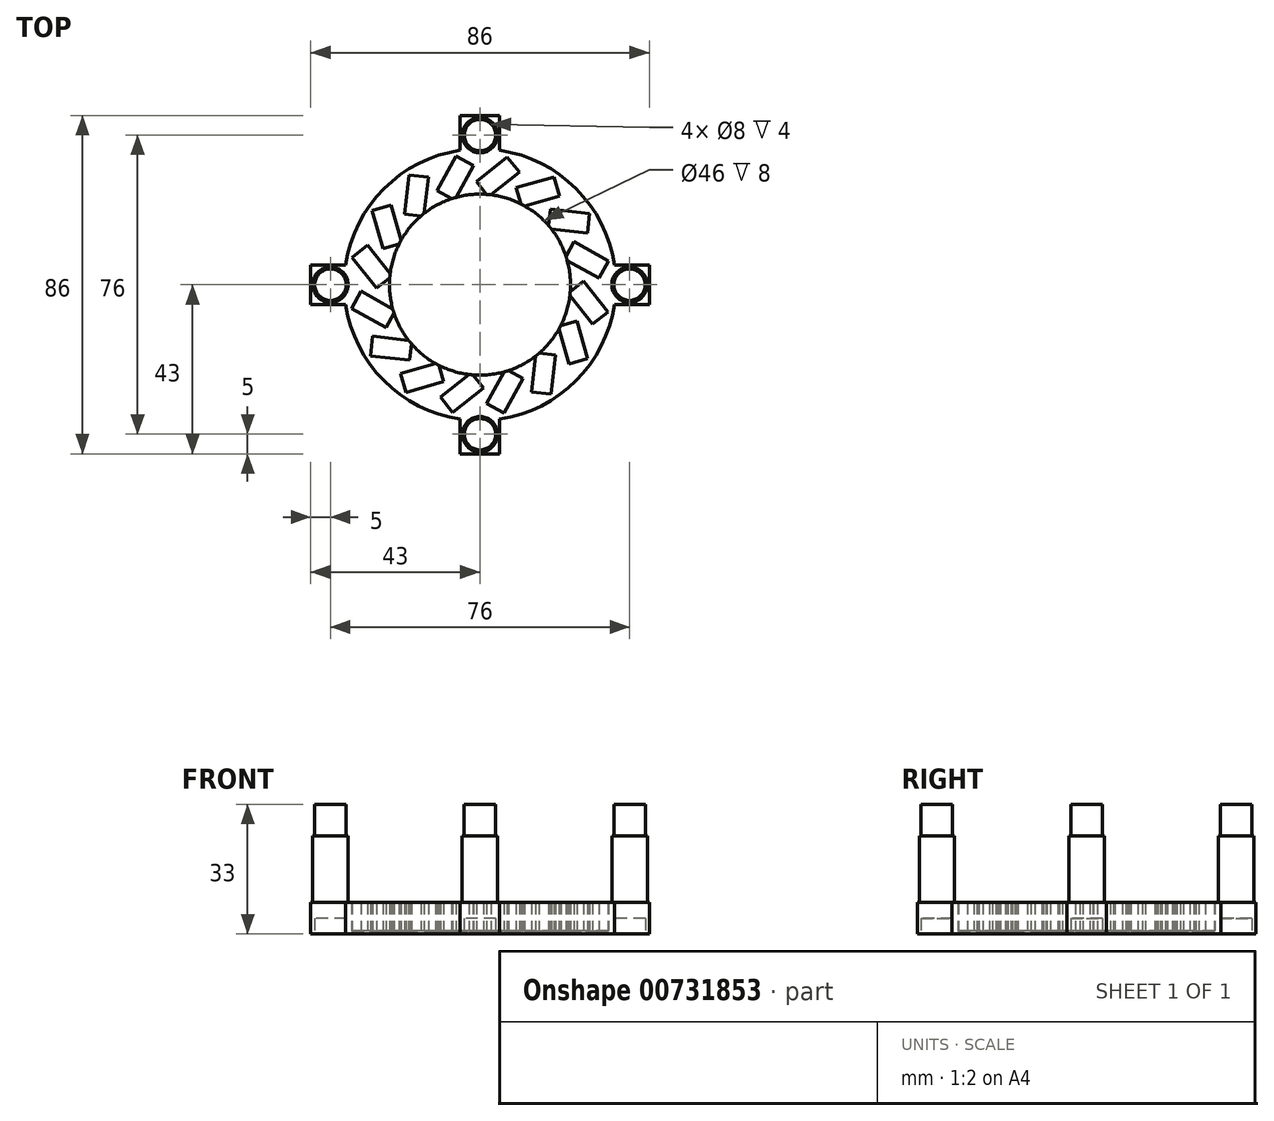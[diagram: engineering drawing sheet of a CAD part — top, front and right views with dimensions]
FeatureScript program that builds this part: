
annotation { "Feature Type Name" : "Feature", "Feature Type Description" : "" }
export const myFeature = defineFeature(function(context is Context, id is Id, definition is map)
    precondition{}
    {
        {
            var Q0;
            Q0=qCreatedBy(makeId("Top.planeOp"),FACE);
            var sketch = newSketch(context, id + "F0", { "sketchPlane" : qUnion([Q0])});
            skCircle(sketch, "E0", {"center": v(0, 0) * mm, "radius": 23 * mm});
            skCircle(sketch, "E1", {"center": v(0, 0) * mm, "radius": 34 * mm});
            skLineSegment(sketch, "E2", {"start": v(0, 0) * mm, "end": v(0.79, 29.99) * mm, "construction": true});
            skLineSegment(sketch, "E3.bottom", {"start": v(8.46, 30.52) * mm, "end": v(10.02, 28.56) * mm});
            skLineSegment(sketch, "E3.top", {"start": v(0.64, 24.3) * mm, "end": v(2.2, 22.34) * mm});
            skLineSegment(sketch, "E3.right", {"start": v(10.02, 28.56) * mm, "end": v(2.2, 22.34) * mm});
            skLineSegment(sketch, "E4.MirrorCS", {"start": v(6.9, 32.47) * mm, "end": v(-0.92, 26.25) * mm});
            skLineSegment(sketch, "E5.MirrorCS", {"start": v(0.64, 24.3) * mm, "end": v(-0.92, 26.25) * mm});
            skLineSegment(sketch, "E6.MirrorCS", {"start": v(8.46, 30.52) * mm, "end": v(6.9, 32.47) * mm});
            skLineSegment(sketch, "E7", {"start": v(0, 0) * mm, "end": v(35, 0) * mm, "construction": true});
            skPoint(sketch, "E8", {"position": v(0.6, 23) * mm});
            skSolve(sketch);
        }
        {
            var Q0;
            Q0=qCreatedBy(makeId("Top.planeOp"),FACE);
            var sketch = newSketch(context, id + "F1", { "sketchPlane" : qUnion([Q0])});
            skArc(sketch, "E9", {"start": v(-34.4, -2.7) * mm, "mid": v(-24.4, -24.4) * mm, "end": v(-2.7, -34.4) * mm});
            skCircle(sketch, "E10", {"center": v(0, 0) * mm, "radius": 23 * mm});
            skArc(sketch, "E11", {"start": v(-33.94, -1.95) * mm, "mid": v(-24.04, -24.04) * mm, "end": v(-1.95, -33.94) * mm});
            skLineSegment(sketch, "E12", {"start": v(0, 0) * mm, "end": v(34, 0) * mm, "construction": true});
            skCircle(sketch, "E13", {"center": v(0, 38) * mm, "radius": 4 * mm});
            skCircle(sketch, "E14", {"center": v(0, 38) * mm, "radius": 4.5 * mm});
            skLineSegment(sketch, "E15", {"start": v(0, 42.5) * mm, "end": v(0, 43) * mm});
            skLineSegment(sketch, "E16", {"start": v(0, 43) * mm, "end": v(5, 43) * mm});
            skLineSegment(sketch, "E17", {"start": v(5, 43) * mm, "end": v(5, 34.14) * mm});
            skLineSegment(sketch, "E18.MirrorCS", {"start": v(0, 43) * mm, "end": v(-5, 43) * mm});
            skLineSegment(sketch, "E19.MirrorCS", {"start": v(-5, 43) * mm, "end": v(-5, 34.14) * mm});
            skLineSegment(sketch, "E20.1.0", {"start": v(-43, 0) * mm, "end": v(-43, 5) * mm});
            skLineSegment(sketch, "E20.1.1", {"start": v(-43, 5) * mm, "end": v(-34.14, 5) * mm});
            skLineSegment(sketch, "E20.1.2", {"start": v(-43, 0) * mm, "end": v(-43, -5) * mm});
            skLineSegment(sketch, "E20.1.3", {"start": v(-43, -5) * mm, "end": v(-34.14, -5) * mm});
            skCircle(sketch, "E20.1.4", {"center": v(-38, 0) * mm, "radius": 4.5 * mm});
            skCircle(sketch, "E20.1.5", {"center": v(-38, 0) * mm, "radius": 4 * mm});
            skLineSegment(sketch, "E20.2.0", {"start": v(0, -43) * mm, "end": v(-5, -43) * mm});
            skLineSegment(sketch, "E20.2.1", {"start": v(-5, -43) * mm, "end": v(-5, -34.14) * mm});
            skLineSegment(sketch, "E20.2.2", {"start": v(0, -43) * mm, "end": v(5, -43) * mm});
            skLineSegment(sketch, "E20.2.3", {"start": v(5, -43) * mm, "end": v(5, -34.14) * mm});
            skCircle(sketch, "E20.2.4", {"center": v(0, -38) * mm, "radius": 4.5 * mm});
            skCircle(sketch, "E20.2.5", {"center": v(0, -38) * mm, "radius": 4 * mm});
            skLineSegment(sketch, "E20.3.0", {"start": v(43, 0) * mm, "end": v(43, -5) * mm});
            skLineSegment(sketch, "E20.3.1", {"start": v(43, -5) * mm, "end": v(34.14, -5) * mm});
            skLineSegment(sketch, "E20.3.2", {"start": v(43, 0) * mm, "end": v(43, 5) * mm});
            skLineSegment(sketch, "E20.3.3", {"start": v(43, 5) * mm, "end": v(34.14, 5) * mm});
            skCircle(sketch, "E20.3.4", {"center": v(38, 0) * mm, "radius": 4.5 * mm});
            skCircle(sketch, "E20.3.5", {"center": v(38, 0) * mm, "radius": 4 * mm});
            skArc(sketch, "E21.trimOffspring", {"start": v(33.94, 1.95) * mm, "mid": v(24.04, 24.04) * mm, "end": v(1.95, 33.94) * mm});
            skArc(sketch, "E22.trimOffspring", {"start": v(34.4, 2.7) * mm, "mid": v(24.4, 24.4) * mm, "end": v(2.7, 34.4) * mm});
            skArc(sketch, "E23.trimOffspring", {"start": v(-2.7, 34.4) * mm, "mid": v(-24.4, 24.4) * mm, "end": v(-34.4, 2.7) * mm});
            skArc(sketch, "E24.trimOffspring", {"start": v(2.7, -34.4) * mm, "mid": v(24.4, -24.4) * mm, "end": v(34.4, -2.7) * mm});
            skArc(sketch, "E25.trimOffspring", {"start": v(1.95, -33.94) * mm, "mid": v(24.04, -24.04) * mm, "end": v(33.94, -1.95) * mm});
            skArc(sketch, "E26.trimOffspring", {"start": v(-1.95, 33.94) * mm, "mid": v(-24.04, 24.04) * mm, "end": v(-33.94, 1.95) * mm});
            skLineSegment(sketch, "E27.0.0", {"start": v(-0.92, 26.25) * mm, "end": v(0.64, 24.3) * mm});
            skLineSegment(sketch, "E27.0.1", {"start": v(0.64, 24.3) * mm, "end": v(1.71, 22.94) * mm});
            skLineSegment(sketch, "E27.0.3", {"start": v(2.81, 22.83) * mm, "end": v(10.02, 28.56) * mm});
            skLineSegment(sketch, "E27.0.4", {"start": v(10.02, 28.56) * mm, "end": v(8.46, 30.52) * mm});
            skLineSegment(sketch, "E27.0.5", {"start": v(8.46, 30.52) * mm, "end": v(6.9, 32.47) * mm});
            skLineSegment(sketch, "E27.0.6", {"start": v(6.9, 32.47) * mm, "end": v(-0.92, 26.25) * mm});
            skLineSegment(sketch, "E28.0.0", {"start": v(2.2, 22.34) * mm, "end": v(2.81, 22.83) * mm});
            skLineSegment(sketch, "E28.0.2", {"start": v(1.71, 22.94) * mm, "end": v(2.2, 22.34) * mm});
            skLineSegment(sketch, "E29.1.0", {"start": v(-6.05, 32.64) * mm, "end": v(-10.9, 23.9) * mm});
            skLineSegment(sketch, "E29.1.1", {"start": v(-3.86, 31.43) * mm, "end": v(-6.05, 32.64) * mm});
            skLineSegment(sketch, "E29.1.2", {"start": v(-1.67, 30.22) * mm, "end": v(-3.86, 31.43) * mm});
            skLineSegment(sketch, "E29.1.3", {"start": v(-6.14, 22.17) * mm, "end": v(-1.67, 30.22) * mm});
            skLineSegment(sketch, "E29.1.4", {"start": v(-8.7, 22.69) * mm, "end": v(-7.2, 21.85) * mm});
            skLineSegment(sketch, "E29.1.5", {"start": v(-10.9, 23.9) * mm, "end": v(-8.7, 22.69) * mm});
            skLineSegment(sketch, "E29.1.6", {"start": v(-6.52, 21.47) * mm, "end": v(-6.14, 22.17) * mm});
            skLineSegment(sketch, "E29.1.7", {"start": v(-7.2, 21.85) * mm, "end": v(-6.52, 21.47) * mm});
            skLineSegment(sketch, "E29.2.0", {"start": v(-18.08, 27.85) * mm, "end": v(-19.21, 17.9) * mm});
            skLineSegment(sketch, "E29.2.1", {"start": v(-15.6, 27.56) * mm, "end": v(-18.08, 27.85) * mm});
            skLineSegment(sketch, "E29.2.2", {"start": v(-13.11, 27.28) * mm, "end": v(-15.6, 27.56) * mm});
            skLineSegment(sketch, "E29.2.3", {"start": v(-14.15, 18.13) * mm, "end": v(-13.11, 27.28) * mm});
            skLineSegment(sketch, "E29.2.4", {"start": v(-16.73, 17.63) * mm, "end": v(-15, 17.43) * mm});
            skLineSegment(sketch, "E29.2.5", {"start": v(-19.21, 17.9) * mm, "end": v(-16.73, 17.63) * mm});
            skLineSegment(sketch, "E29.2.6", {"start": v(-14.24, 17.34) * mm, "end": v(-14.15, 18.13) * mm});
            skLineSegment(sketch, "E29.2.7", {"start": v(-15, 17.43) * mm, "end": v(-14.24, 17.34) * mm});
            skLineSegment(sketch, "E29.3.0", {"start": v(-27.36, 18.8) * mm, "end": v(-24.6, 9.2) * mm});
            skLineSegment(sketch, "E29.3.1", {"start": v(-24.96, 19.5) * mm, "end": v(-27.36, 18.8) * mm});
            skLineSegment(sketch, "E29.3.2", {"start": v(-22.55, 20.19) * mm, "end": v(-24.96, 19.5) * mm});
            skLineSegment(sketch, "E29.3.3", {"start": v(-20.01, 11.33) * mm, "end": v(-22.55, 20.19) * mm});
            skLineSegment(sketch, "E29.3.4", {"start": v(-22.2, 9.88) * mm, "end": v(-20.53, 10.36) * mm});
            skLineSegment(sketch, "E29.3.5", {"start": v(-24.6, 9.2) * mm, "end": v(-22.2, 9.88) * mm});
            skLineSegment(sketch, "E29.3.6", {"start": v(-19.8, 10.57) * mm, "end": v(-20.01, 11.33) * mm});
            skLineSegment(sketch, "E29.3.7", {"start": v(-20.53, 10.36) * mm, "end": v(-19.8, 10.57) * mm});
            skLineSegment(sketch, "E29.4.0", {"start": v(-32.47, 6.9) * mm, "end": v(-26.25, -0.92) * mm});
            skLineSegment(sketch, "E29.4.1", {"start": v(-30.52, 8.46) * mm, "end": v(-32.47, 6.9) * mm});
            skLineSegment(sketch, "E29.4.2", {"start": v(-28.56, 10.02) * mm, "end": v(-30.52, 8.46) * mm});
            skLineSegment(sketch, "E29.4.3", {"start": v(-22.83, 2.81) * mm, "end": v(-28.56, 10.02) * mm});
            skLineSegment(sketch, "E29.4.4", {"start": v(-24.3, 0.64) * mm, "end": v(-22.94, 1.71) * mm});
            skLineSegment(sketch, "E29.4.5", {"start": v(-26.25, -0.92) * mm, "end": v(-24.3, 0.64) * mm});
            skLineSegment(sketch, "E29.4.6", {"start": v(-22.34, 2.2) * mm, "end": v(-22.83, 2.81) * mm});
            skLineSegment(sketch, "E29.4.7", {"start": v(-22.94, 1.71) * mm, "end": v(-22.34, 2.2) * mm});
            skLineSegment(sketch, "E29.5.0", {"start": v(-32.64, -6.05) * mm, "end": v(-23.9, -10.9) * mm});
            skLineSegment(sketch, "E29.5.1", {"start": v(-31.43, -3.86) * mm, "end": v(-32.64, -6.05) * mm});
            skLineSegment(sketch, "E29.5.2", {"start": v(-30.22, -1.67) * mm, "end": v(-31.43, -3.86) * mm});
            skLineSegment(sketch, "E29.5.3", {"start": v(-22.17, -6.14) * mm, "end": v(-30.22, -1.67) * mm});
            skLineSegment(sketch, "E29.5.4", {"start": v(-22.69, -8.7) * mm, "end": v(-21.85, -7.2) * mm});
            skLineSegment(sketch, "E29.5.5", {"start": v(-23.9, -10.9) * mm, "end": v(-22.69, -8.7) * mm});
            skLineSegment(sketch, "E29.5.6", {"start": v(-21.47, -6.52) * mm, "end": v(-22.17, -6.14) * mm});
            skLineSegment(sketch, "E29.5.7", {"start": v(-21.85, -7.2) * mm, "end": v(-21.47, -6.52) * mm});
            skLineSegment(sketch, "E29.6.0", {"start": v(-27.85, -18.08) * mm, "end": v(-17.9, -19.21) * mm});
            skLineSegment(sketch, "E29.6.1", {"start": v(-27.56, -15.6) * mm, "end": v(-27.85, -18.08) * mm});
            skLineSegment(sketch, "E29.6.2", {"start": v(-27.28, -13.11) * mm, "end": v(-27.56, -15.6) * mm});
            skLineSegment(sketch, "E29.6.3", {"start": v(-18.13, -14.15) * mm, "end": v(-27.28, -13.11) * mm});
            skLineSegment(sketch, "E29.6.4", {"start": v(-17.63, -16.73) * mm, "end": v(-17.43, -15) * mm});
            skLineSegment(sketch, "E29.6.5", {"start": v(-17.9, -19.21) * mm, "end": v(-17.63, -16.73) * mm});
            skLineSegment(sketch, "E29.6.6", {"start": v(-17.34, -14.24) * mm, "end": v(-18.13, -14.15) * mm});
            skLineSegment(sketch, "E29.6.7", {"start": v(-17.43, -15) * mm, "end": v(-17.34, -14.24) * mm});
            skLineSegment(sketch, "E29.7.0", {"start": v(-18.8, -27.36) * mm, "end": v(-9.2, -24.6) * mm});
            skLineSegment(sketch, "E29.7.1", {"start": v(-19.5, -24.96) * mm, "end": v(-18.8, -27.36) * mm});
            skLineSegment(sketch, "E29.7.2", {"start": v(-20.19, -22.55) * mm, "end": v(-19.5, -24.96) * mm});
            skLineSegment(sketch, "E29.7.3", {"start": v(-11.33, -20.01) * mm, "end": v(-20.19, -22.55) * mm});
            skLineSegment(sketch, "E29.7.4", {"start": v(-9.88, -22.2) * mm, "end": v(-10.36, -20.53) * mm});
            skLineSegment(sketch, "E29.7.5", {"start": v(-9.2, -24.6) * mm, "end": v(-9.88, -22.2) * mm});
            skLineSegment(sketch, "E29.7.6", {"start": v(-10.57, -19.8) * mm, "end": v(-11.33, -20.01) * mm});
            skLineSegment(sketch, "E29.7.7", {"start": v(-10.36, -20.53) * mm, "end": v(-10.57, -19.8) * mm});
            skLineSegment(sketch, "E29.8.0", {"start": v(-6.9, -32.47) * mm, "end": v(0.92, -26.25) * mm});
            skLineSegment(sketch, "E29.8.1", {"start": v(-8.46, -30.52) * mm, "end": v(-6.9, -32.47) * mm});
            skLineSegment(sketch, "E29.8.2", {"start": v(-10.02, -28.56) * mm, "end": v(-8.46, -30.52) * mm});
            skLineSegment(sketch, "E29.8.3", {"start": v(-2.81, -22.83) * mm, "end": v(-10.02, -28.56) * mm});
            skLineSegment(sketch, "E29.8.4", {"start": v(-0.64, -24.3) * mm, "end": v(-1.71, -22.94) * mm});
            skLineSegment(sketch, "E29.8.5", {"start": v(0.92, -26.25) * mm, "end": v(-0.64, -24.3) * mm});
            skLineSegment(sketch, "E29.8.6", {"start": v(-2.2, -22.34) * mm, "end": v(-2.81, -22.83) * mm});
            skLineSegment(sketch, "E29.8.7", {"start": v(-1.71, -22.94) * mm, "end": v(-2.2, -22.34) * mm});
            skLineSegment(sketch, "E29.9.0", {"start": v(6.05, -32.64) * mm, "end": v(10.9, -23.9) * mm});
            skLineSegment(sketch, "E29.9.1", {"start": v(3.86, -31.43) * mm, "end": v(6.05, -32.64) * mm});
            skLineSegment(sketch, "E29.9.2", {"start": v(1.67, -30.22) * mm, "end": v(3.86, -31.43) * mm});
            skLineSegment(sketch, "E29.9.3", {"start": v(6.14, -22.17) * mm, "end": v(1.67, -30.22) * mm});
            skLineSegment(sketch, "E29.9.4", {"start": v(8.7, -22.69) * mm, "end": v(7.2, -21.85) * mm});
            skLineSegment(sketch, "E29.9.5", {"start": v(10.9, -23.9) * mm, "end": v(8.7, -22.69) * mm});
            skLineSegment(sketch, "E29.9.6", {"start": v(6.52, -21.47) * mm, "end": v(6.14, -22.17) * mm});
            skLineSegment(sketch, "E29.9.7", {"start": v(7.2, -21.85) * mm, "end": v(6.52, -21.47) * mm});
            skLineSegment(sketch, "E29.10.0", {"start": v(18.08, -27.85) * mm, "end": v(19.21, -17.9) * mm});
            skLineSegment(sketch, "E29.10.1", {"start": v(15.6, -27.56) * mm, "end": v(18.08, -27.85) * mm});
            skLineSegment(sketch, "E29.10.2", {"start": v(13.11, -27.28) * mm, "end": v(15.6, -27.56) * mm});
            skLineSegment(sketch, "E29.10.3", {"start": v(14.15, -18.13) * mm, "end": v(13.11, -27.28) * mm});
            skLineSegment(sketch, "E29.10.4", {"start": v(16.73, -17.63) * mm, "end": v(15, -17.43) * mm});
            skLineSegment(sketch, "E29.10.5", {"start": v(19.21, -17.9) * mm, "end": v(16.73, -17.63) * mm});
            skLineSegment(sketch, "E29.10.6", {"start": v(14.24, -17.34) * mm, "end": v(14.15, -18.13) * mm});
            skLineSegment(sketch, "E29.10.7", {"start": v(15, -17.43) * mm, "end": v(14.24, -17.34) * mm});
            skLineSegment(sketch, "E29.11.0", {"start": v(27.36, -18.8) * mm, "end": v(24.6, -9.2) * mm});
            skLineSegment(sketch, "E29.11.1", {"start": v(24.96, -19.5) * mm, "end": v(27.36, -18.8) * mm});
            skLineSegment(sketch, "E29.11.2", {"start": v(22.55, -20.19) * mm, "end": v(24.96, -19.5) * mm});
            skLineSegment(sketch, "E29.11.3", {"start": v(20.01, -11.33) * mm, "end": v(22.55, -20.19) * mm});
            skLineSegment(sketch, "E29.11.4", {"start": v(22.2, -9.88) * mm, "end": v(20.53, -10.36) * mm});
            skLineSegment(sketch, "E29.11.5", {"start": v(24.6, -9.2) * mm, "end": v(22.2, -9.88) * mm});
            skLineSegment(sketch, "E29.11.6", {"start": v(19.8, -10.57) * mm, "end": v(20.01, -11.33) * mm});
            skLineSegment(sketch, "E29.11.7", {"start": v(20.53, -10.36) * mm, "end": v(19.8, -10.57) * mm});
            skLineSegment(sketch, "E29.12.0", {"start": v(32.47, -6.9) * mm, "end": v(26.25, 0.92) * mm});
            skLineSegment(sketch, "E29.12.1", {"start": v(30.52, -8.46) * mm, "end": v(32.47, -6.9) * mm});
            skLineSegment(sketch, "E29.12.2", {"start": v(28.56, -10.02) * mm, "end": v(30.52, -8.46) * mm});
            skLineSegment(sketch, "E29.12.3", {"start": v(22.83, -2.81) * mm, "end": v(28.56, -10.02) * mm});
            skLineSegment(sketch, "E29.12.4", {"start": v(24.3, -0.64) * mm, "end": v(22.94, -1.71) * mm});
            skLineSegment(sketch, "E29.12.5", {"start": v(26.25, 0.92) * mm, "end": v(24.3, -0.64) * mm});
            skLineSegment(sketch, "E29.12.6", {"start": v(22.34, -2.2) * mm, "end": v(22.83, -2.81) * mm});
            skLineSegment(sketch, "E29.12.7", {"start": v(22.94, -1.71) * mm, "end": v(22.34, -2.2) * mm});
            skLineSegment(sketch, "E29.13.0", {"start": v(32.64, 6.05) * mm, "end": v(23.9, 10.9) * mm});
            skLineSegment(sketch, "E29.13.1", {"start": v(31.43, 3.86) * mm, "end": v(32.64, 6.05) * mm});
            skLineSegment(sketch, "E29.13.2", {"start": v(30.22, 1.67) * mm, "end": v(31.43, 3.86) * mm});
            skLineSegment(sketch, "E29.13.3", {"start": v(22.17, 6.14) * mm, "end": v(30.22, 1.67) * mm});
            skLineSegment(sketch, "E29.13.4", {"start": v(22.69, 8.7) * mm, "end": v(21.85, 7.2) * mm});
            skLineSegment(sketch, "E29.13.5", {"start": v(23.9, 10.9) * mm, "end": v(22.69, 8.7) * mm});
            skLineSegment(sketch, "E29.13.6", {"start": v(21.47, 6.52) * mm, "end": v(22.17, 6.14) * mm});
            skLineSegment(sketch, "E29.13.7", {"start": v(21.85, 7.2) * mm, "end": v(21.47, 6.52) * mm});
            skLineSegment(sketch, "E29.14.0", {"start": v(27.85, 18.08) * mm, "end": v(17.9, 19.21) * mm});
            skLineSegment(sketch, "E29.14.1", {"start": v(27.56, 15.6) * mm, "end": v(27.85, 18.08) * mm});
            skLineSegment(sketch, "E29.14.2", {"start": v(27.28, 13.11) * mm, "end": v(27.56, 15.6) * mm});
            skLineSegment(sketch, "E29.14.3", {"start": v(18.13, 14.15) * mm, "end": v(27.28, 13.11) * mm});
            skLineSegment(sketch, "E29.14.4", {"start": v(17.63, 16.73) * mm, "end": v(17.43, 15) * mm});
            skLineSegment(sketch, "E29.14.5", {"start": v(17.9, 19.21) * mm, "end": v(17.63, 16.73) * mm});
            skLineSegment(sketch, "E29.14.6", {"start": v(17.34, 14.24) * mm, "end": v(18.13, 14.15) * mm});
            skLineSegment(sketch, "E29.14.7", {"start": v(17.43, 15) * mm, "end": v(17.34, 14.24) * mm});
            skLineSegment(sketch, "E29.15.0", {"start": v(18.8, 27.36) * mm, "end": v(9.2, 24.6) * mm});
            skLineSegment(sketch, "E29.15.1", {"start": v(19.5, 24.96) * mm, "end": v(18.8, 27.36) * mm});
            skLineSegment(sketch, "E29.15.2", {"start": v(20.19, 22.55) * mm, "end": v(19.5, 24.96) * mm});
            skLineSegment(sketch, "E29.15.3", {"start": v(11.33, 20.01) * mm, "end": v(20.19, 22.55) * mm});
            skLineSegment(sketch, "E29.15.4", {"start": v(9.88, 22.2) * mm, "end": v(10.36, 20.53) * mm});
            skLineSegment(sketch, "E29.15.5", {"start": v(9.2, 24.6) * mm, "end": v(9.88, 22.2) * mm});
            skLineSegment(sketch, "E29.15.6", {"start": v(10.57, 19.8) * mm, "end": v(11.33, 20.01) * mm});
            skLineSegment(sketch, "E29.15.7", {"start": v(10.36, 20.53) * mm, "end": v(10.57, 19.8) * mm});
            skSolve(sketch);
        }
        {
            var Q0;
            Q0=qSketchRegion(id+"F1",true);
            var Q1;
            Q1=makeQuery(id+"F1.imprint","IMPRINT",FACE,{"disambiguationData":[TD([[makeQuery(id+"F1.imprint","IMPRINT",EDGE,{"derivedFrom":sQuery(id+"F1.wireOp",EDGE,"d15ed5a5-fd29-49d6-a964-e686c6378fca.3.5")}),1.0]])]});
            var Q2;
            Q2=makeQuery(id+"F1.imprint","IMPRINT",FACE,{"disambiguationData":[TD([[makeQuery(id+"F1.imprint","IMPRINT",EDGE,{"derivedFrom":sQuery(id+"F1.wireOp",EDGE,"d15ed5a5-fd29-49d6-a964-e686c6378fca.3.4")}),1.0]])]});
            var Q3;
            Q3=makeQuery(id+"F1.imprint","IMPRINT",FACE,{"disambiguationData":[TD([[makeQuery(id+"F1.imprint","IMPRINT",EDGE,{"derivedFrom":sQuery(id+"F1.wireOp",EDGE,"nMKEX2UH-BGaZ-hXa7-XY8u-qAvmxy0yM5Br")}),1.0]])]});
            var Q4;
            Q4=makeQuery(id+"F1.imprint","IMPRINT",FACE,{"disambiguationData":[TD([[makeQuery(id+"F1.imprint","IMPRINT",EDGE,{"derivedFrom":sQuery(id+"F1.wireOp",EDGE,"nMKEX2UH-BGaZ-hXa7-XY8u-qAvmxy0yM5Br")}),-1.0]])]});
            var Q5;
            Q5=makeQuery(id+"F1.imprint","IMPRINT",FACE,{"disambiguationData":[TD([[makeQuery(id+"F1.imprint","IMPRINT",EDGE,{"derivedFrom":sQuery(id+"F1.wireOp",EDGE,"d15ed5a5-fd29-49d6-a964-e686c6378fca.1.5")}),1.0]])]});
            var Q6;
            Q6=makeQuery(id+"F1.imprint","IMPRINT",FACE,{"disambiguationData":[TD([[makeQuery(id+"F1.imprint","IMPRINT",EDGE,{"derivedFrom":sQuery(id+"F1.wireOp",EDGE,"d15ed5a5-fd29-49d6-a964-e686c6378fca.1.4")}),1.0]])]});
            var Q7;
            Q7=makeQuery(id+"F1.imprint","IMPRINT",FACE,{"disambiguationData":[TD([[makeQuery(id+"F1.imprint","IMPRINT",EDGE,{"derivedFrom":sQuery(id+"F1.wireOp",EDGE,"d15ed5a5-fd29-49d6-a964-e686c6378fca.2.5")}),1.0]])]});
            var Q8;
            Q8=makeQuery(id+"F1.imprint","IMPRINT",FACE,{"disambiguationData":[TD([[makeQuery(id+"F1.imprint","IMPRINT",EDGE,{"derivedFrom":sQuery(id+"F1.wireOp",EDGE,"d15ed5a5-fd29-49d6-a964-e686c6378fca.2.4")}),1.0]])]});
            var Q9;
            {var subQ98=sQuery(id+"F1.wireOp",EDGE,"f3e762ff-506c-4368-bb15-f758a9c07f8b.bottom");Q9=makeQuery(id+"F1.imprint","IMPRINT",FACE,{"disambiguationData":[TD([[makeQuery(id+"F1.imprint","IMPRINT",EDGE,{"derivedFrom":subQ98}),1.0]])]});}
            var Q10;
            {var subQ16=sQuery(id+"F1.wireOp",EDGE,"E11");Q10=makeQuery(id+"F1.imprint","IMPRINT",FACE,{"disambiguationData":[TD([[makeQuery(id+"F1.imprint","IMPRINT",EDGE,{"derivedFrom":subQ16}),1.0]])]});}
            extrude(context, id + "F2", {"entities" : qUnion([Q0, Q1, Q2, Q3, Q4, Q5, Q6, Q7, Q8, Q9, Q10]), "depth" : 8 * mm, "offsetDistance" : 25 * mm});
        }
        {
            var Q0;
            Q0=makeQuery(id+"F1.imprint","IMPRINT",FACE,{"disambiguationData":[TD([[makeQuery(id+"F1.imprint","IMPRINT",EDGE,{"derivedFrom":sQuery(id+"F1.wireOp",EDGE,"E13")}),1.0]])]});
            var Q1;
            Q1=makeQuery(id+"F1.imprint","IMPRINT",FACE,{"disambiguationData":[TD([[makeQuery(id+"F1.imprint","IMPRINT",EDGE,{"derivedFrom":sQuery(id+"F1.wireOp",EDGE,"E20.3.5")}),1.0]])]});
            var Q2;
            Q2=makeQuery(id+"F1.imprint","IMPRINT",FACE,{"disambiguationData":[TD([[makeQuery(id+"F1.imprint","IMPRINT",EDGE,{"derivedFrom":sQuery(id+"F1.wireOp",EDGE,"E13")}),-1.0]])]});
            var Q3;
            Q3=makeQuery(id+"F1.imprint","IMPRINT",FACE,{"disambiguationData":[TD([[makeQuery(id+"F1.imprint","IMPRINT",EDGE,{"derivedFrom":sQuery(id+"F1.wireOp",EDGE,"E20.3.5")}),-1.0]])]});
            var Q4;
            Q4=makeQuery(id+"F1.imprint","IMPRINT",FACE,{"disambiguationData":[TD([[makeQuery(id+"F1.imprint","IMPRINT",EDGE,{"derivedFrom":sQuery(id+"F1.wireOp",EDGE,"E20.2.5")}),1.0]])]});
            var Q5;
            Q5=makeQuery(id+"F1.imprint","IMPRINT",FACE,{"disambiguationData":[TD([[makeQuery(id+"F1.imprint","IMPRINT",EDGE,{"derivedFrom":sQuery(id+"F1.wireOp",EDGE,"E20.2.5")}),-1.0]])]});
            var Q6;
            Q6=makeQuery(id+"F1.imprint","IMPRINT",FACE,{"disambiguationData":[TD([[makeQuery(id+"F1.imprint","IMPRINT",EDGE,{"derivedFrom":sQuery(id+"F1.wireOp",EDGE,"E20.1.5")}),1.0]])]});
            var Q7;
            Q7=makeQuery(id+"F1.imprint","IMPRINT",FACE,{"disambiguationData":[TD([[makeQuery(id+"F1.imprint","IMPRINT",EDGE,{"derivedFrom":sQuery(id+"F1.wireOp",EDGE,"E20.1.5")}),-1.0]])]});
            extrude(context, id + "F3", {"entities" : qUnion([Q0, Q1, Q2, Q3, Q4, Q5, Q6, Q7]), "operationType" : NewBodyOperationType.ADD, "depth" : 25 * mm, "offsetDistance" : 25 * mm});
        }
        {
            var Q0;
            Q0=makeQuery(id+"F1.imprint","IMPRINT",FACE,{"disambiguationData":[TD([[makeQuery(id+"F1.imprint","IMPRINT",EDGE,{"derivedFrom":sQuery(id+"F1.wireOp",EDGE,"d15ed5a5-fd29-49d6-a964-e686c6378fca.1.5")}),1.0]])]});
            var Q1;
            Q1=makeQuery(id+"F1.imprint","IMPRINT",FACE,{"disambiguationData":[TD([[makeQuery(id+"F1.imprint","IMPRINT",EDGE,{"derivedFrom":sQuery(id+"F1.wireOp",EDGE,"d15ed5a5-fd29-49d6-a964-e686c6378fca.3.5")}),1.0]])]});
            var Q2;
            Q2=makeQuery(id+"F1.imprint","IMPRINT",FACE,{"disambiguationData":[TD([[makeQuery(id+"F1.imprint","IMPRINT",EDGE,{"derivedFrom":sQuery(id+"F1.wireOp",EDGE,"d15ed5a5-fd29-49d6-a964-e686c6378fca.2.5")}),1.0]])]});
            var Q3;
            Q3=makeQuery(id+"F1.imprint","IMPRINT",FACE,{"disambiguationData":[TD([[makeQuery(id+"F1.imprint","IMPRINT",EDGE,{"derivedFrom":sQuery(id+"F1.wireOp",EDGE,"nMKEX2UH-BGaZ-hXa7-XY8u-qAvmxy0yM5Br")}),1.0]])]});
            var Q4;
            Q4=makeQuery(id+"F1.imprint","IMPRINT",FACE,{"disambiguationData":[TD([[makeQuery(id+"F1.imprint","IMPRINT",EDGE,{"derivedFrom":sQuery(id+"F1.wireOp",EDGE,"E20.3.5")}),1.0]])]});
            var Q5;
            Q5=makeQuery(id+"F1.imprint","IMPRINT",FACE,{"disambiguationData":[TD([[makeQuery(id+"F1.imprint","IMPRINT",EDGE,{"derivedFrom":sQuery(id+"F1.wireOp",EDGE,"E20.2.5")}),1.0]])]});
            var Q6;
            Q6=makeQuery(id+"F1.imprint","IMPRINT",FACE,{"disambiguationData":[TD([[makeQuery(id+"F1.imprint","IMPRINT",EDGE,{"derivedFrom":sQuery(id+"F1.wireOp",EDGE,"E13")}),1.0]])]});
            var Q7;
            Q7=makeQuery(id+"F1.imprint","IMPRINT",FACE,{"disambiguationData":[TD([[makeQuery(id+"F1.imprint","IMPRINT",EDGE,{"derivedFrom":sQuery(id+"F1.wireOp",EDGE,"E20.1.5")}),1.0]])]});
            extrude(context, id + "F4", {"entities" : qUnion([Q0, Q1, Q2, Q3, Q4, Q5, Q6, Q7]), "operationType" : NewBodyOperationType.ADD, "depth" : 33 * mm, "offsetDistance" : 25 * mm});
        }
        {
            var Q0;
            Q0=makeQuery(id+"F1.imprint","IMPRINT",FACE,{"disambiguationData":[TD([[makeQuery(id+"F1.imprint","IMPRINT",EDGE,{"derivedFrom":sQuery(id+"F1.wireOp",EDGE,"nMKEX2UH-BGaZ-hXa7-XY8u-qAvmxy0yM5Br")}),1.0]])]});
            var Q1;
            Q1=makeQuery(id+"F1.imprint","IMPRINT",FACE,{"disambiguationData":[TD([[makeQuery(id+"F1.imprint","IMPRINT",EDGE,{"derivedFrom":sQuery(id+"F1.wireOp",EDGE,"d15ed5a5-fd29-49d6-a964-e686c6378fca.1.5")}),1.0]])]});
            var Q2;
            Q2=makeQuery(id+"F1.imprint","IMPRINT",FACE,{"disambiguationData":[TD([[makeQuery(id+"F1.imprint","IMPRINT",EDGE,{"derivedFrom":sQuery(id+"F1.wireOp",EDGE,"d15ed5a5-fd29-49d6-a964-e686c6378fca.3.5")}),1.0]])]});
            var Q3;
            Q3=makeQuery(id+"F1.imprint","IMPRINT",FACE,{"disambiguationData":[TD([[makeQuery(id+"F1.imprint","IMPRINT",EDGE,{"derivedFrom":sQuery(id+"F1.wireOp",EDGE,"d15ed5a5-fd29-49d6-a964-e686c6378fca.2.5")}),1.0]])]});
            var Q4;
            Q4=makeQuery(id+"F1.imprint","IMPRINT",FACE,{"disambiguationData":[TD([[makeQuery(id+"F1.imprint","IMPRINT",EDGE,{"derivedFrom":sQuery(id+"F1.wireOp",EDGE,"E20.1.5")}),1.0]])]});
            var Q5;
            Q5=makeQuery(id+"F1.imprint","IMPRINT",FACE,{"disambiguationData":[TD([[makeQuery(id+"F1.imprint","IMPRINT",EDGE,{"derivedFrom":sQuery(id+"F1.wireOp",EDGE,"E20.3.5")}),1.0]])]});
            var Q6;
            Q6=makeQuery(id+"F1.imprint","IMPRINT",FACE,{"disambiguationData":[TD([[makeQuery(id+"F1.imprint","IMPRINT",EDGE,{"derivedFrom":sQuery(id+"F1.wireOp",EDGE,"E13")}),1.0]])]});
            var Q7;
            Q7=makeQuery(id+"F1.imprint","IMPRINT",FACE,{"disambiguationData":[TD([[makeQuery(id+"F1.imprint","IMPRINT",EDGE,{"derivedFrom":sQuery(id+"F1.wireOp",EDGE,"E20.2.5")}),1.0]])]});
            extrude(context, id + "F5", {"entities" : qUnion([Q0, Q1, Q2, Q3, Q4, Q5, Q6, Q7]), "operationType" : NewBodyOperationType.REMOVE, "depth" : 4 * mm, "offsetDistance" : 25 * mm});
        }
        {
            var Q0;
            Q0=makeQuery(id+"F0.imprint","IMPRINT",FACE,{"disambiguationData":[TD([[makeQuery(id+"F0.imprint","IMPRINT",EDGE,{"derivedFrom":sQuery(id+"F0.wireOp",EDGE,"E1")}),1.0]])]});
            var Q1;
            {var subQ1=sQuery(id+"F1.wireOp",EDGE,"f3e762ff-506c-4368-bb15-f758a9c07f8b.bottom");Q1=makeQuery(id+"F1.imprint","IMPRINT",FACE,{"disambiguationData":[TD([[makeQuery(id+"F1.imprint","IMPRINT",EDGE,{"derivedFrom":subQ1}),-1.0]])]});}
            var Q2;
            {var subQ1=sQuery(id+"F0.wireOp",EDGE,"E3.bottom");Q2=makeQuery(id+"F0.imprint","IMPRINT",FACE,{"disambiguationData":[TD([[makeQuery(id+"F0.imprint","IMPRINT",EDGE,{"derivedFrom":subQ1}),-1.0]])]});}
            extrude(context, id + "F6", {"entities" : qUnion([Q0, Q1, Q2]), "operationType" : NewBodyOperationType.ADD, "depth" : 0.8 * mm, "offsetDistance" : 25 * mm});
        }
    });
